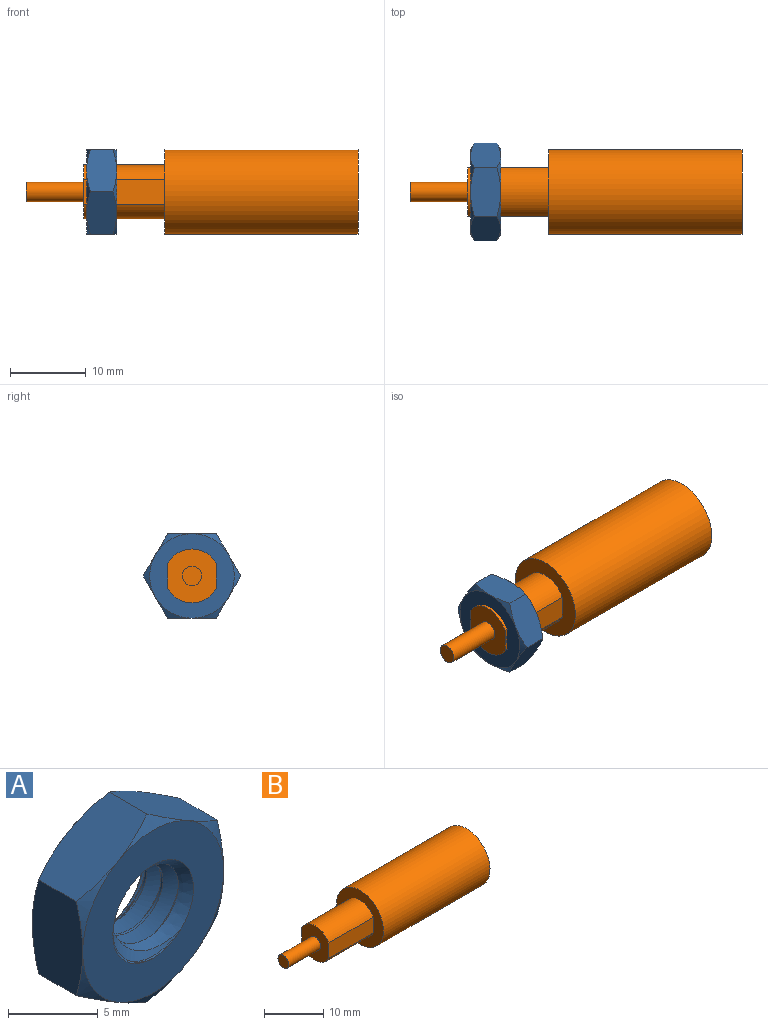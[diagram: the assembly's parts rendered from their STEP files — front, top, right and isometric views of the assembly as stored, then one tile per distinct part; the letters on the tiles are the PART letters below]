
ASSEMBLY  parts=2 mates=1
PART A: 26 faces, bbox 13.4x5.6x13.4 mm
  f0: cone r=5.56mm half-angle=60deg, axis (0,1,0), area 3mm2, adj f11,f12,f15
  f1: cone r=3.17mm half-angle=45deg, axis (0,-1,0), area 10.5mm2, adj f5,f6,f7,f15
  f2: cone r=5.56mm half-angle=60deg, axis (0,-1,0), area 3mm2, adj f8,f11,f12
  f3: cone r=3.17mm half-angle=45deg, axis (0,1,0), area 10.5mm2, adj f5,f6,f7,f8
  f4: cylinder r=3.17mm len=6.35mm, axis (0,-1,0), area 9.9mm2, adj f5,f7,f8,f15
  f5: bspline ~6.35x6.35mm, area 41.5mm2, adj f1,f3,f4,f6
  f6: cylinder r=2.35mm len=4.7mm, axis (0,-1,0), area 4.3mm2, adj f1,f3,f5,f7
  f7: bspline ~6.35x6.35mm, area 41.5mm2, adj f1,f3,f4,f6
  f8: plane 11.11x11.11mm, normal (0,1,0), area 65.3mm2, adj f2,f3,f4,f16,f17,f18,f19,f20
  f9: plane 6.08x4.5mm, normal (-0.5,0,-0.87), area 23.3mm2, adj f10,f14,f16,f20,f23,f24
  f10: plane 6.95x4.5mm, normal (-1,0,0), area 23.3mm2, adj f9,f11,f19,f20,f24,f25
  f11: plane 6.08x4.5mm, normal (-0.5,0,0.87), area 23.3mm2, adj f0,f2,f10,f12,f19,f25
  f12: plane 6.08x4.5mm, normal (0.5,0,0.87), area 23.3mm2, adj f0,f2,f11,f13,f18,f21
  f13: plane 6.95x4.5mm, normal (1,0,0), area 23.3mm2, adj f12,f14,f17,f18,f21,f22
  f14: plane 6.08x4.5mm, normal (0.5,0,-0.87), area 23.3mm2, adj f9,f13,f16,f17,f22,f23
  f15: plane 11.11x11.11mm, normal (0,-1,0), area 65.3mm2, adj f0,f1,f4,f21,f22,f23,f24,f25
  f16: cone r=5.56mm half-angle=60deg, axis (0,-1,0), area 3mm2, adj f8,f9,f14
  f17: cone r=5.56mm half-angle=60deg, axis (0,-1,0), area 3mm2, adj f8,f13,f14
  f18: cone r=5.56mm half-angle=60deg, axis (0,-1,0), area 3mm2, adj f8,f12,f13
  f19: cone r=5.56mm half-angle=60deg, axis (0,-1,0), area 3mm2, adj f8,f10,f11
  f20: cone r=5.56mm half-angle=60deg, axis (0,-1,0), area 3mm2, adj f8,f9,f10
  f21: cone r=5.56mm half-angle=60deg, axis (0,1,0), area 3mm2, adj f12,f13,f15
  f22: cone r=5.56mm half-angle=60deg, axis (0,1,0), area 3mm2, adj f13,f14,f15
  f23: cone r=5.56mm half-angle=60deg, axis (0,1,0), area 3mm2, adj f9,f14,f15
  f24: cone r=5.56mm half-angle=60deg, axis (0,1,0), area 3mm2, adj f9,f10,f15
  f25: cone r=5.56mm half-angle=60deg, axis (0,1,0), area 3mm2, adj f10,f11,f15
PART B: 12 faces, bbox 43.7x11.2x11.2 mm
  f0: plane 11.18x11.18mm, normal (-1,0,0), area 60mm2, adj f1,f3,f4,f5,f6
  f1: cylinder r=5.59mm len=25.4mm, axis (-1,0,0), area 891.8mm2, adj f0,f2
  f2: plane 11.18x11.18mm, normal (1,0,0), area 85.1mm2, adj f1,f8
  f3: cylinder r=3.56mm len=10.67mm, axis (1,0,0), area 83.7mm2, adj f0,f4,f6,f7
  f4: plane 10.67x3.2mm, normal (0,1,0), area 34.2mm2, adj f0,f3,f5,f7
  f5: cylinder r=3.56mm len=10.67mm, axis (1,0,0), area 83.7mm2, adj f0,f4,f6,f7
  f6: plane 10.67x3.2mm, normal (0,-1,0), area 34.2mm2, adj f0,f3,f5,f7
  f7: plane 7.11x6.35mm, normal (-1,0,0), area 33mm2, adj f3,f4,f5,f6,f10
  f8: cylinder r=2.03mm len=8.38mm, axis (1,0,0), area 107mm2, adj f2,f9
  f9: plane 4.06x4.06mm, normal (1,0,0), area 13mm2, adj f8
  f10: cylinder r=1.27mm len=7.62mm, axis (1,0,0), area 60.8mm2, adj f7,f11
  f11: plane 2.54x2.54mm, normal (-1,0,0), area 5.1mm2, adj f10
PLACE A rot(axis=(0.58,-0.58,0.58),120deg) t=(-8.33,0,0)mm
PLACE B at identity fixed
MATE cylindrical B.f8 <-> A.f0  axis (-1,0,0) through (0,0,0)mm
